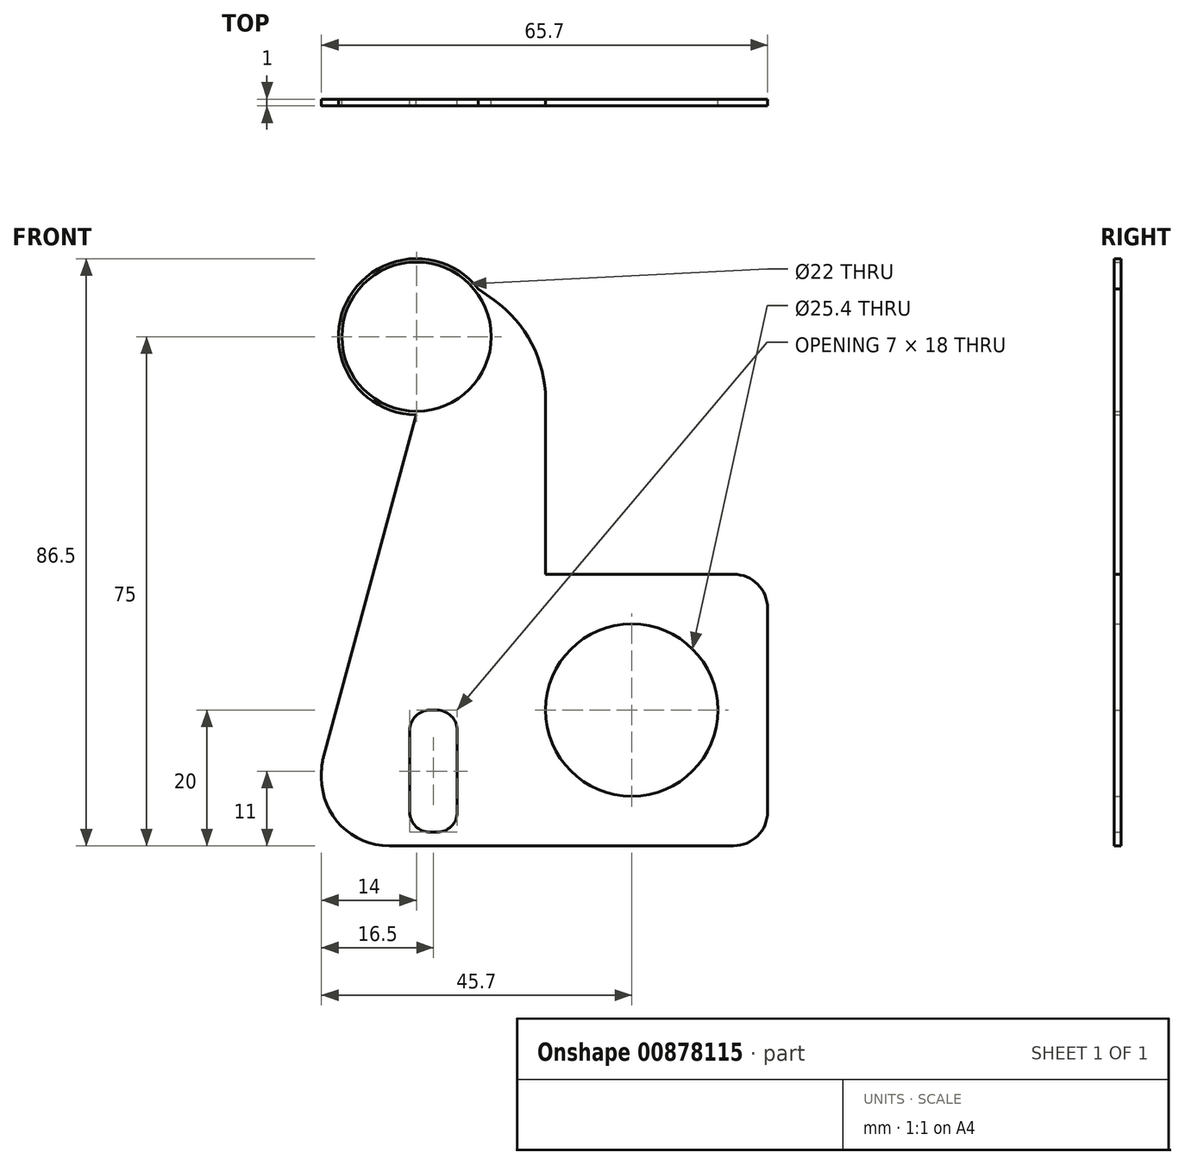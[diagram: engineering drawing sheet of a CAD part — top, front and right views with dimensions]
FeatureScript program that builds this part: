
annotation { "Feature Type Name" : "Feature", "Feature Type Description" : "" }
export const myFeature = defineFeature(function(context is Context, id is Id, definition is map)
    precondition{}
    {
        {
            var Q0;
            Q0=qCreatedBy(makeId("Front.planeOp"),FACE);
            var sketch = newSketch(context, id + "F0", { "sketchPlane" : qUnion([Q0])});
            skCircle(sketch, "E0", {"center": v(0, 0) * mm, "radius": 12.7 * mm});
            skLineSegment(sketch, "E1.bottom", {"start": v(15, 20) * mm, "end": v(-20, 20) * mm});
            skLineSegment(sketch, "E1.top", {"start": v(15, -20) * mm, "end": v(-20, -20) * mm});
            skLineSegment(sketch, "E1.left", {"start": v(20, 15) * mm, "end": v(20, -15) * mm});
            skLineSegment(sketch, "E1.right", {"start": v(-20, 20) * mm, "end": v(-20, -20) * mm});
            skLineSegment(sketch, "E2", {"start": v(0, 0) * mm, "end": v(-20, 0) * mm, "construction": true});
            skPoint(sketch, "E3", {"position": v(-12.7, 0) * mm});
            skLineSegment(sketch, "E4", {"start": v(-12.7, 0) * mm, "end": v(-12.7, 20) * mm, "construction": true});
            skLineSegment(sketch, "E5", {"start": v(-12.7, 0) * mm, "end": v(-12.7, -20) * mm, "construction": true});
            skLineSegment(sketch, "E6", {"start": v(-29.2, -20) * mm, "end": v(-29.2, -9) * mm, "construction": true});
            skLineSegment(sketch, "E7.bottom", {"start": v(-29.7, 0) * mm, "end": v(-28.7, 0) * mm});
            skLineSegment(sketch, "E7.top", {"start": v(-29.7, -18) * mm, "end": v(-28.7, -18) * mm});
            skLineSegment(sketch, "E7.left", {"start": v(-32.7, -3) * mm, "end": v(-32.7, -15) * mm});
            skLineSegment(sketch, "E7.right", {"start": v(-25.7, -3) * mm, "end": v(-25.7, -15) * mm});
            skPoint(sketch, "E7.middle", {"position": v(-29.2, -9) * mm});
            skPoint(sketch, "E8.visualSharp", {"position": v(-32.7, 0) * mm});
            skArc(sketch, "E8.filletArc", {"start": v(-29.7, 0) * mm, "mid": v(-31.82, -0.88) * mm, "end": v(-32.7, -3) * mm});
            skPoint(sketch, "E9.visualSharp", {"position": v(-25.7, 0) * mm});
            skArc(sketch, "E9.filletArc", {"start": v(-25.7, -3) * mm, "mid": v(-26.58, -0.88) * mm, "end": v(-28.7, 0) * mm});
            skPoint(sketch, "E10.visualSharp", {"position": v(-25.7, -18) * mm});
            skArc(sketch, "E10.filletArc", {"start": v(-28.7, -18) * mm, "mid": v(-26.58, -17.12) * mm, "end": v(-25.7, -15) * mm});
            skPoint(sketch, "E11.visualSharp", {"position": v(-32.7, -18) * mm});
            skArc(sketch, "E11.filletArc", {"start": v(-32.7, -15) * mm, "mid": v(-31.82, -17.12) * mm, "end": v(-29.7, -18) * mm});
            skLineSegment(sketch, "E12", {"start": v(-12.7, 55) * mm, "end": v(-31.7, 55) * mm, "construction": true});
            skCircle(sketch, "E13", {"center": v(-31.7, 55) * mm, "radius": 11 * mm});
            skCircle(sketch, "E14", {"center": v(-31.7, 55) * mm, "radius": 11.5 * mm});
            skLineSegment(sketch, "E15", {"start": v(-31.77, 43.5) * mm, "end": v(-45.35, -6.67) * mm});
            skLineSegment(sketch, "E16", {"start": v(-45.7, -9.29) * mm, "end": v(-45.7, -10) * mm});
            skLineSegment(sketch, "E17", {"start": v(-12.7, -20) * mm, "end": v(-12.7, 45.7) * mm});
            skLineSegment(sketch, "E18", {"start": v(-20.28, 60.38) * mm, "end": v(-22.6, 62.03) * mm});
            skPoint(sketch, "E19.visualSharp", {"position": v(-12.7, 55) * mm});
            skArc(sketch, "E19.filletArc", {"start": v(-12.7, 45.7) * mm, "mid": v(-14.7, 53.96) * mm, "end": v(-20.28, 60.38) * mm});
            skLineSegment(sketch, "E20", {"start": v(-35.7, -20) * mm, "end": v(-20, -20) * mm});
            skPoint(sketch, "E21.visualSharp", {"position": v(-45.7, -7.96) * mm});
            skArc(sketch, "E21.filletArc", {"start": v(-45.35, -6.67) * mm, "mid": v(-45.61, -7.97) * mm, "end": v(-45.7, -9.29) * mm});
            skPoint(sketch, "E22.visualSharp", {"position": v(-45.7, -20) * mm});
            skArc(sketch, "E22.filletArc", {"start": v(-45.7, -10) * mm, "mid": v(-42.77, -17.07) * mm, "end": v(-35.7, -20) * mm});
            skPoint(sketch, "E23.visualSharp", {"position": v(20, 20) * mm});
            skArc(sketch, "E23.filletArc", {"start": v(20, 15) * mm, "mid": v(18.54, 18.54) * mm, "end": v(15, 20) * mm});
            skPoint(sketch, "E24.visualSharp", {"position": v(20, -20) * mm});
            skArc(sketch, "E24.filletArc", {"start": v(15, -20) * mm, "mid": v(18.54, -18.54) * mm, "end": v(20, -15) * mm});
            skSolve(sketch);
        }
        {
            var Q0;
            Q0=makeQuery(id+"F0.imprint","IMPRINT",FACE,{"disambiguationData":[TD([[makeQuery(id+"F0.imprint","IMPRINT",EDGE,{"derivedFrom":sQuery(id+"F0.wireOp",EDGE,"E13")}),-1.0]])]});
            var Q1;
            {var subQ0=sQuery(id+"F0.wireOp",EDGE,"E1.right");Q1=makeQuery(id+"F0.imprint","IMPRINT",FACE,{"disambiguationData":[TD([[makeQuery(id+"F0.imprint","IMPRINT",EDGE,{"derivedFrom":subQ0}),-1.0]])]});}
            var Q2;
            {var subQ7=sQuery(id+"F0.wireOp",EDGE,"E0");Q2=makeQuery(id+"F0.imprint","IMPRINT",FACE,{"disambiguationData":[TD([[makeQuery(id+"F0.imprint","IMPRINT",EDGE,{"derivedFrom":subQ7}),-1.0]])]});}
            var Q3;
            {var subQ4=sQuery(id+"F0.wireOp",EDGE,"E1.right");Q3=makeQuery(id+"F0.imprint","IMPRINT",FACE,{"disambiguationData":[TD([[makeQuery(id+"F0.imprint","IMPRINT",EDGE,{"derivedFrom":subQ4}),1.0]])]});}
            extrude(context, id + "F1", {"entities" : qUnion([Q0, Q1, Q2, Q3]), "depth" : 1 * mm, "offsetDistance" : 25 * mm});
        }
    });
